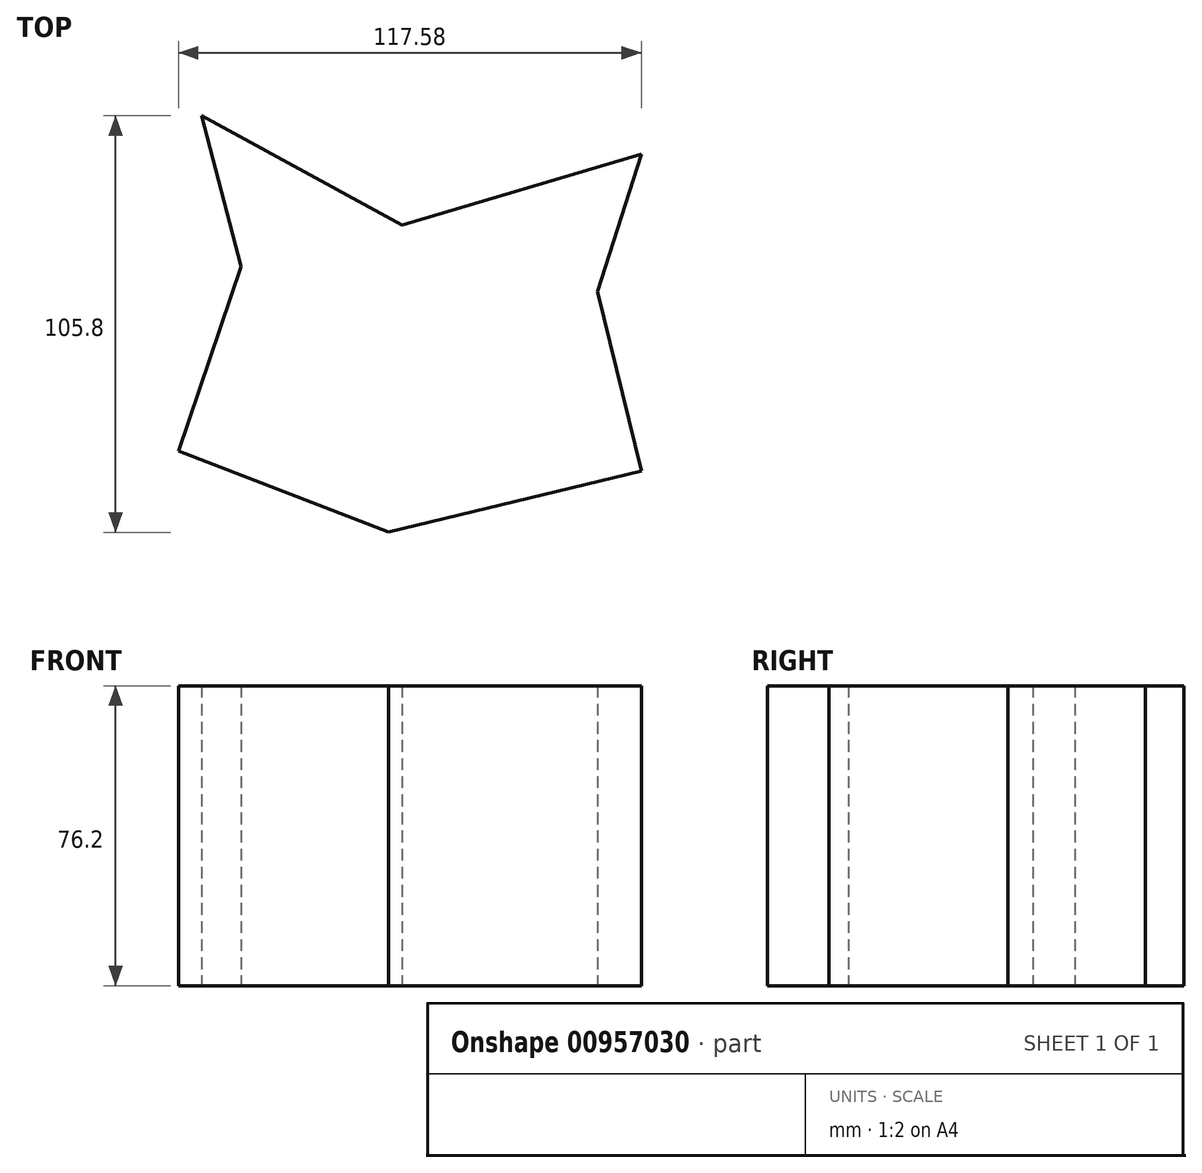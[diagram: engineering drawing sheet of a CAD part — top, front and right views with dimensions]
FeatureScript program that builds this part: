
annotation { "Feature Type Name" : "Feature", "Feature Type Description" : "" }
export const myFeature = defineFeature(function(context is Context, id is Id, definition is map)
    precondition{}
    {
        {
            var Q0;
            Q0=qCreatedBy(makeId("Top.planeOp"),FACE);
            var sketch = newSketch(context, id + "F0", { "sketchPlane" : qUnion([Q0])});
            skLineSegment(sketch, "E0", {"start": v(0, 35.79) * mm, "end": v(-50.87, 63.49) * mm});
            skLineSegment(sketch, "E1", {"start": v(-50.87, 63.49) * mm, "end": v(-40.85, 25.18) * mm});
            skLineSegment(sketch, "E2", {"start": v(-40.85, 25.18) * mm, "end": v(-56.76, -21.68) * mm});
            skLineSegment(sketch, "E3", {"start": v(-56.76, -21.68) * mm, "end": v(-3.42, -42.3) * mm});
            skLineSegment(sketch, "E4", {"start": v(-3.42, -42.3) * mm, "end": v(60.82, -26.69) * mm});
            skLineSegment(sketch, "E5", {"start": v(60.82, -26.69) * mm, "end": v(49.74, 18.88) * mm});
            skLineSegment(sketch, "E6", {"start": v(49.74, 18.88) * mm, "end": v(60.82, 53.76) * mm});
            skLineSegment(sketch, "E7", {"start": v(60.82, 53.76) * mm, "end": v(0, 35.79) * mm});
            skSolve(sketch);
        }
        {
            var Q0;
            Q0 = qSketchRegion(id + "F0", true);
            extrude(context, id + "F1", {"entities" : qUnion([Q0]), "depth" : 76.2 * mm, "offsetDistance" : 25.4 * mm});
        }
    });
